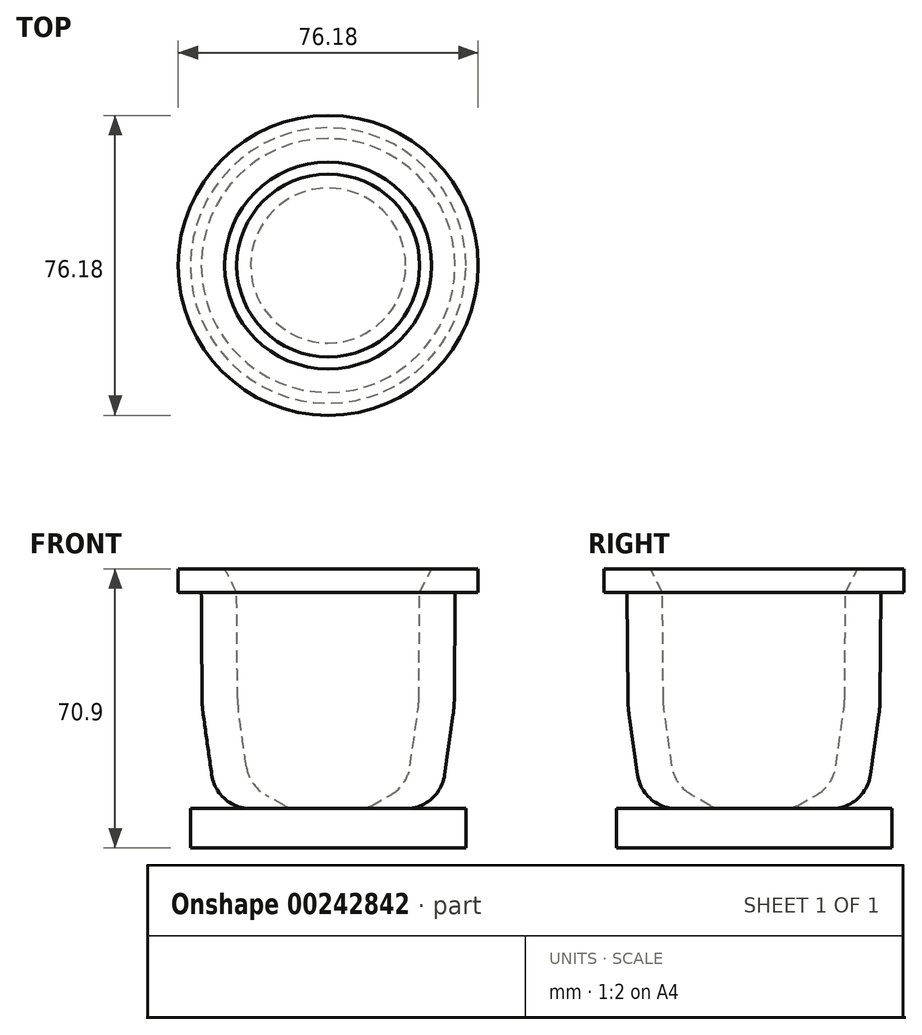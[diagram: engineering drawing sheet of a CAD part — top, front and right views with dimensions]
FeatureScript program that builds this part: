
annotation { "Feature Type Name" : "Feature", "Feature Type Description" : "" }
export const myFeature = defineFeature(function(context is Context, id is Id, definition is map)
    precondition{}
    {
        {
            var Q0;
            Q0=qCreatedBy(makeId("Top.planeOp"),FACE);
            var sketch = newSketch(context, id + "F0", { "sketchPlane" : qUnion([Q0])});
            skCircle(sketch, "E0", {"center": v(0, 0) * mm, "radius": 35 * mm});
            skSolve(sketch);
        }
        {
            var Q0;
            Q0 = qSketchRegion(id + "F0", true);
            extrude(context, id + "F1", {"entities" : qUnion([Q0]), "depth" : 10 * mm});
        }
        {
            var Q0;
            Q0=qCreatedBy(makeId("Front.planeOp"),FACE);
            var sketch = newSketch(context, id + "F2", { "sketchPlane" : qUnion([Q0])});
            skLineSegment(sketch, "E1", {"start": v(-38.1, 70.9) * mm, "end": v(-38.1, 64.87) * mm});
            skLineSegment(sketch, "E2", {"start": v(-38.1, 64.87) * mm, "end": v(-32.24, 64.87) * mm});
            skLineSegment(sketch, "E3", {"start": v(-32.24, 64.87) * mm, "end": v(-32.04, 37.9) * mm});
            skLineSegment(sketch, "E4", {"start": v(-31.75, 33.96) * mm, "end": v(-29.6, 18.6) * mm});
            skPoint(sketch, "E5.visualSharp", {"position": v(-32.03, 35.92) * mm});
            skArc(sketch, "E5.filletArc", {"start": v(-32.04, 37.9) * mm, "mid": v(-31.96, 35.93) * mm, "end": v(-31.75, 33.96) * mm});
            skPoint(sketch, "E6.start.orphan", {"position": v(0, 70.9) * mm});
            skLineSegment(sketch, "E7", {"start": v(-38.1, 70.9) * mm, "end": v(-26.28, 70.9) * mm});
            skLineSegment(sketch, "E8", {"start": v(0, -18.5) * mm, "end": v(0, 74.52) * mm, "construction": true});
            skArc(sketch, "E9.filletArc", {"start": v(-29.6, 18.6) * mm, "mid": v(-26.25, 12.45) * mm, "end": v(-19.7, 10) * mm});
            skPoint(sketch, "E10.visualSharp", {"position": v(-24.52, 11.24) * mm});
            skLineSegment(sketch, "E11", {"start": v(-19.7, 10) * mm, "end": v(0, 10) * mm});
            skLineSegment(sketch, "E12.1", {"start": v(-22.84, 35.2) * mm, "end": v(-20.81, 20.78) * mm});
            skArc(sketch, "E12.2", {"start": v(-23.04, 37.98) * mm, "mid": v(-22.99, 36.59) * mm, "end": v(-22.84, 35.2) * mm});
            skLineSegment(sketch, "E12.3", {"start": v(-23.24, 64.94) * mm, "end": v(-23.04, 37.98) * mm});
            skLineSegment(sketch, "E13", {"start": v(-26.28, 70.9) * mm, "end": v(-23.24, 64.94) * mm});
            skLineSegment(sketch, "E14", {"start": v(-15.92, 13.52) * mm, "end": v(-11, 10.67) * mm});
            skLineSegment(sketch, "E15", {"start": v(-8.5, 10) * mm, "end": v(0, 10) * mm});
            skPoint(sketch, "E16.visualSharp", {"position": v(-9.85, 10) * mm});
            skArc(sketch, "E16.filletArc", {"start": v(-11, 10.67) * mm, "mid": v(-9.8, 10.17) * mm, "end": v(-8.5, 10) * mm});
            skPoint(sketch, "E17.visualSharp", {"position": v(-20.13, 15.96) * mm});
            skArc(sketch, "E17.filletArc", {"start": v(-20.81, 20.78) * mm, "mid": v(-19.2, 16.6) * mm, "end": v(-15.92, 13.52) * mm});
            skSolve(sketch);
        }
        {
            var Q0;
            Q0=makeQuery(id+"F2.imprint","IMPRINT",FACE,{"disambiguationData":[TD([[makeQuery(id+"F2.imprint","IMPRINT",EDGE,{"derivedFrom":sQuery(id+"F2.wireOp",EDGE,"E1")}),1.0]])]});
            var Q1;
            Q1=sQuery(id+"F2.wireOp",EDGE,"E8");
            revolve(context, id + "F3", {"operationType" : NewBodyOperationType.ADD, "entities" : qUnion([Q0]), "axis" : qUnion([Q1]), "revolveType" : RevolveType.FULL});
        }
    });
